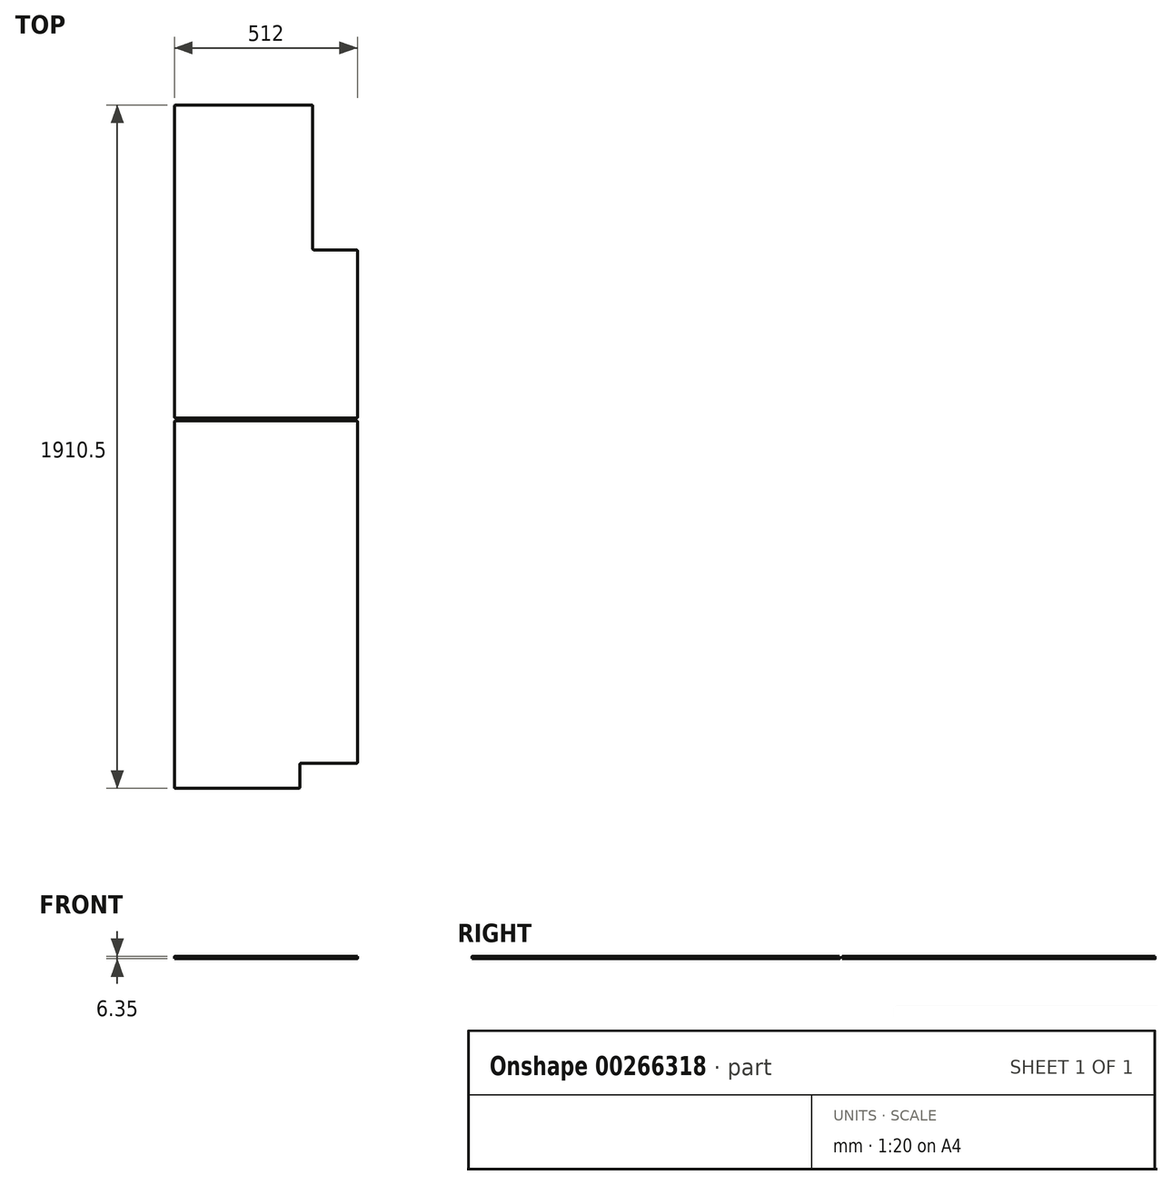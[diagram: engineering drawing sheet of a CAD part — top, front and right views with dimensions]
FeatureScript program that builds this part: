
annotation { "Feature Type Name" : "Feature", "Feature Type Description" : "" }
export const myFeature = defineFeature(function(context is Context, id is Id, definition is map)
    precondition{}
    {
        {
            var Q0;
            Q0=qCreatedBy(makeId("Top.planeOp"),FACE);
            var sketch = newSketch(context, id + "F0", { "sketchPlane" : qUnion([Q0])});
            skLineSegment(sketch, "E0.bottom", {"start": v(256, -955.25) * mm, "end": v(-256, -955.25) * mm});
            skLineSegment(sketch, "E0.top", {"start": v(256, 955.25) * mm, "end": v(-256, 955.25) * mm});
            skLineSegment(sketch, "E0.left", {"start": v(256, -955.25) * mm, "end": v(256, 955.25) * mm});
            skLineSegment(sketch, "E0.right", {"start": v(-256, -955.25) * mm, "end": v(-256, 955.25) * mm});
            skPoint(sketch, "E0.middle", {"position": v(0, 0) * mm});
            skLineSegment(sketch, "E1", {"start": v(-256, 72.75) * mm, "end": v(256, 72.75) * mm});
            skLineSegment(sketch, "E2", {"start": v(-256, 80.25) * mm, "end": v(256, 80.25) * mm});
            skLineSegment(sketch, "E3", {"start": v(256, -885.25) * mm, "end": v(95, -885.25) * mm});
            skLineSegment(sketch, "E4", {"start": v(95, -885.25) * mm, "end": v(95, -955.25) * mm});
            skLineSegment(sketch, "E5", {"start": v(131, 955.25) * mm, "end": v(131, 550.25) * mm});
            skLineSegment(sketch, "E6", {"start": v(131, 550.25) * mm, "end": v(256, 550.25) * mm});
            skSolve(sketch);
        }
        {
            var Q0;
            {var subQ3=sQuery(id+"F0.wireOp",EDGE,"E2");Q0=makeQuery(id+"F0.imprint","IMPRINT",FACE,{"disambiguationData":[TD([[makeQuery(id+"F0.imprint","IMPRINT",EDGE,{"derivedFrom":subQ3}),1.0]])]});}
            extrude(context, id + "F1", {"entities" : qUnion([Q0]), "depth" : 6.35 * mm});
        }
        {
            var Q0;
            {var subQ0=sQuery(id+"F0.wireOp",EDGE,"E1");Q0=makeQuery(id+"F0.imprint","IMPRINT",FACE,{"disambiguationData":[TD([[makeQuery(id+"F0.imprint","IMPRINT",EDGE,{"derivedFrom":subQ0}),-1.0]])]});}
            extrude(context, id + "F2", {"entities" : qUnion([Q0]), "depth" : 6.35 * mm});
        }
        {
            var Q0;
            Q0=makeQuery(id+"F2.opExtrude","SWEPT_EDGE",EDGE,{"disambiguationData":[OSD([sQuery(id+"F0.wireOp",EDGE,"E3"),sQuery(id+"F0.wireOp",EDGE,"E4")])]});
            var Q1;
            Q1=makeQuery(id+"F2.opExtrude","SWEPT_EDGE",EDGE,{"disambiguationData":[OSD([sQuery(id+"F0.wireOp",EDGE,"E0.left"),sQuery(id+"F0.wireOp",EDGE,"E3")])]});
            var Q2;
            Q2=makeQuery(id+"F2.opExtrude","SWEPT_EDGE",EDGE,{"disambiguationData":[OSD([sQuery(id+"F0.wireOp",EDGE,"E0.bottom"),sQuery(id+"F0.wireOp",EDGE,"E4")])]});
            var Q3;
            Q3=makeQuery(id+"F2.opExtrude","SWEPT_EDGE",EDGE,{"disambiguationData":[OSD([sQuery(id+"F0.wireOp",EDGE,"E0.bottom"),sQuery(id+"F0.wireOp",EDGE,"E0.right")])]});
            var Q4;
            Q4=makeQuery(id+"F1.opExtrude","SWEPT_EDGE",EDGE,{"disambiguationData":[OSD([sQuery(id+"F0.wireOp",EDGE,"E0.right"),sQuery(id+"F0.wireOp",EDGE,"E2")])]});
            var Q5;
            Q5=makeQuery(id+"F1.opExtrude","SWEPT_EDGE",EDGE,{"disambiguationData":[OSD([sQuery(id+"F0.wireOp",EDGE,"E0.left"),sQuery(id+"F0.wireOp",EDGE,"E2")])]});
            var Q6;
            Q6=makeQuery(id+"F2.opExtrude","SWEPT_EDGE",EDGE,{"disambiguationData":[OSD([sQuery(id+"F0.wireOp",EDGE,"E0.left"),sQuery(id+"F0.wireOp",EDGE,"E1")])]});
            var Q7;
            Q7=makeQuery(id+"F1.opExtrude","SWEPT_EDGE",EDGE,{"disambiguationData":[OSD([sQuery(id+"F0.wireOp",EDGE,"E0.left"),sQuery(id+"F0.wireOp",EDGE,"E6")])]});
            var Q8;
            Q8=makeQuery(id+"F1.opExtrude","SWEPT_EDGE",EDGE,{"disambiguationData":[OSD([sQuery(id+"F0.wireOp",EDGE,"E0.top"),sQuery(id+"F0.wireOp",EDGE,"E5")])]});
            var Q9;
            Q9=makeQuery(id+"F1.opExtrude","SWEPT_EDGE",EDGE,{"disambiguationData":[OSD([sQuery(id+"F0.wireOp",EDGE,"E5"),sQuery(id+"F0.wireOp",EDGE,"E6")])]});
            var Q10;
            Q10=makeQuery(id+"F2.opExtrude","SWEPT_EDGE",EDGE,{"disambiguationData":[OSD([sQuery(id+"F0.wireOp",EDGE,"E0.right"),sQuery(id+"F0.wireOp",EDGE,"E1")])]});
            var Q11;
            Q11=makeQuery(id+"F1.opExtrude","SWEPT_EDGE",EDGE,{"disambiguationData":[OSD([sQuery(id+"F0.wireOp",EDGE,"E0.top"),sQuery(id+"F0.wireOp",EDGE,"E0.right")])]});
            fillet(context, id + "F3", {"entities" : qUnion([Q0, Q1, Q2, Q3, Q4, Q5, Q6, Q7, Q8, Q9, Q10, Q11]), "radius" : 3 * mm, "tangentPropagation" : true, "allowEdgeOverflow" : false});
        }
    });
